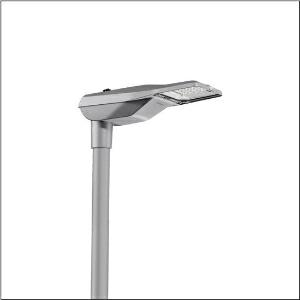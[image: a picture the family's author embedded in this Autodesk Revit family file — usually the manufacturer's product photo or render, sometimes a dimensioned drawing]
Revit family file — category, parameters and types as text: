
# Revit family: streetlight_sl_21_micro___stw1_0a_5xe1e43s08db_ea06
name_source: partatom
category: Lighting Fixtures
units: mm (PartAtom-declared; Revit-internal decimal feet)

## family parameters
Cut with Voids When Loaded = No
Host = Face
Light Source = No
Part Type = Normal
Room Calculation Point = No
Round Connector Dimension = Use Diameter
Shared = No

## types (1)
- --- (1 x LED, 5320 lm, 39.1 W, 4000K)
    Apparent Load = 39 VA
    CIE Flux Codes = 38 75 98 100 100
    Color Rendering = 70
    Color Temperature = 4000K
    Default Elevation = 1800 mm
    Description = Streetlight SL 21 micro, mast luminaire, primary light control with lens, of PMMA, primary optical cover: cover, of toughened safety glass, transparent, light distribution: STW1.0a, light emission: direct distribution, primary light characteristic: asymmetric, installation type: side-entry, post-top, LED, High Power LED, rated luminous flux: 5.320lm, luminous efficacy: 136lm/W, light colour: 740, colour temperature: 4000K, control: flexible luminous flux parameterisation, time-dependent luminous flux control, constant luminous flux control, overheat protection, presetting dimming logarithmic, mains connection: 220..240V, AC, 50/60Hz, start of lifetime: 39W, end of service life: 41W, reduction: 18W, luminaire housing, of diecast aluminium, powder-coated, Siteco® metallic grey (DB 702S), corrosivity category C5 mid according to DIN EN ISO 12944, please order mast flange separately, inclination adjustable: 0°, 5°, 10°, 15°, sealing non-destructively replaceable, multi-level sealing system, length: 528mm, width: 235mm, height: 110mm, mast flange for spigot size: 42mm (side-entry): 5XC10008XM4, 60/48mm (side-entry/post-top): 5XC10108XM2, 76/60mm (side-entry/post-top): 5XC10108XM1, Smart Interface above, protection rating (complete): IP66, insulation class (complete): insulation class II (safety insulation), certification: CE, ENEC, ENEC+, VDE, impact resistance: IK09, permissible operating ambient temperature for outdoor applications: -40..+50°C, standard-compliant lighting for roads and squares, packaging unit: 1 piece

Light Distribution: STW1.0a
    Height = 110 mm
    Lamp = 1 x LED
    Lamp Light Flux = 5320 lm
    Lamp Power = 39.1 W
    Lamp count = 1
    Length = 528 mm
    Luminous efficacy = 136 lm/W
    Manufacturer = Siteco
    ModVariant = No
    Model = 5XE1E43S08DB
    Number of Poles = 1
    OnlyDefault = Yes
    Power Factor = 1
    Product Name = Streetlight SL 21 micro | STW1.0a
    Product group = mast luminaire | pylon top
    ProductGroupID = 6100
    Protection Class = Protection class II
    Protection Degree = IP 66
    RLX_Detail_Level = 1
    RLX_Emergency_Light_Flux = 0 lm
    RLX_Emergency_Type = 0
    RLX_Emergency_Type_DB = No
    RlxData = <blob elided: 98397 chars, md5=1ad0dea6>
    Socket = socket
    Standby Power = 0 W
    System Light Flux = 5320 lm
    System Power = 39 W
    Type Comments = factory setting: luminous flux: 100 % | dim-lin: 254 | 765 mA
    Type Image = l_1277292.jpg
    URL = http://relux.com
    VarID = @adj_105465
    Voltage = 0 V
    Weight = 0.00 kg
    Width = 235 mm

## geometry (parser evidence)
native form markers: Blend x4, Sweep x10
no freeform markers — native parametric forms only
